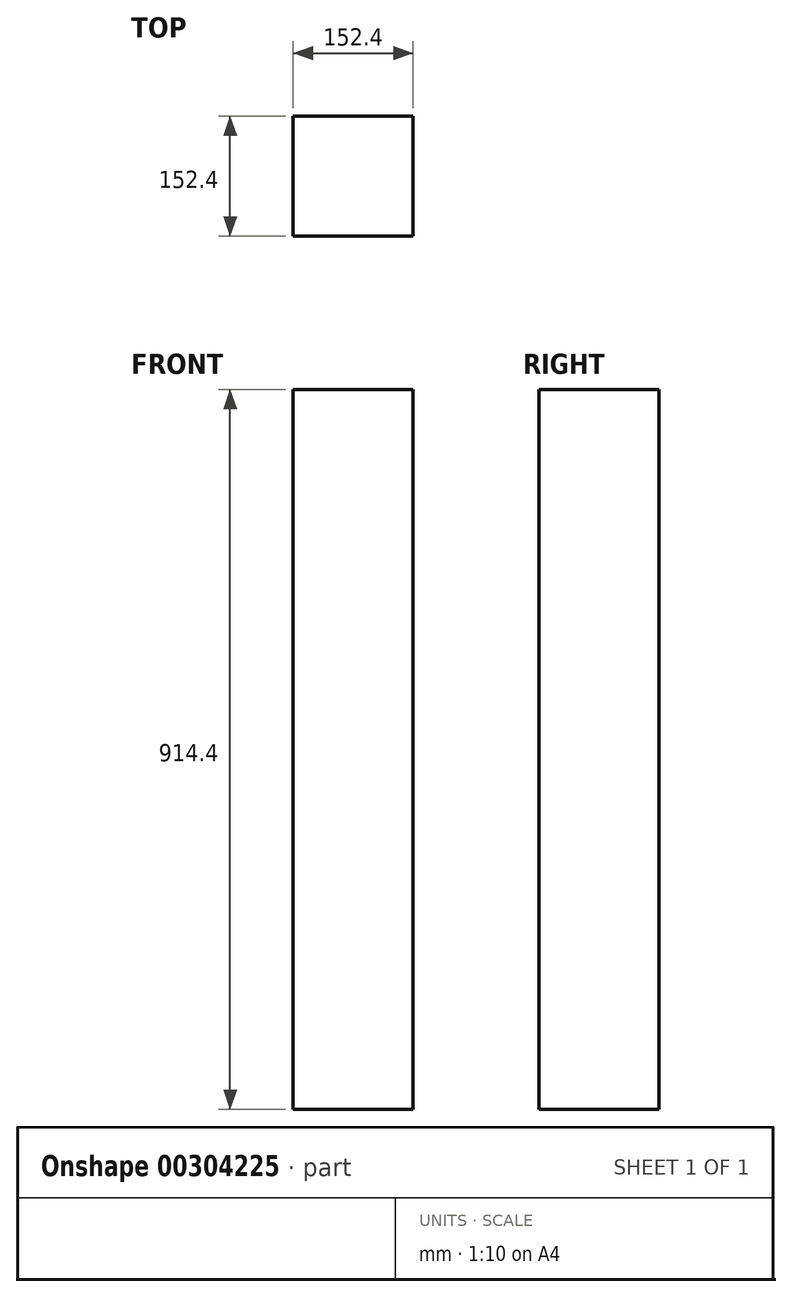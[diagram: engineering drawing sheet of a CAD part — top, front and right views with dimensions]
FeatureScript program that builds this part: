
annotation { "Feature Type Name" : "Feature", "Feature Type Description" : "" }
export const myFeature = defineFeature(function(context is Context, id is Id, definition is map)
    precondition{}
    {
        {
            var Q0;
            Q0=qCreatedBy(makeId("Top.planeOp"),FACE);
            var sketch = newSketch(context, id + "F0", { "sketchPlane" : qUnion([Q0])});
            skLineSegment(sketch, "E0.bottom", {"start": v(-76.2, -76.2) * mm, "end": v(76.2, -76.2) * mm});
            skLineSegment(sketch, "E0.top", {"start": v(-76.2, 76.2) * mm, "end": v(76.2, 76.2) * mm});
            skLineSegment(sketch, "E0.left", {"start": v(-76.2, -76.2) * mm, "end": v(-76.2, 76.2) * mm});
            skLineSegment(sketch, "E0.right", {"start": v(76.2, -76.2) * mm, "end": v(76.2, 76.2) * mm});
            skPoint(sketch, "E0.middle", {"position": v(0, 0) * mm});
            skSolve(sketch);
        }
        {
            var Q0;
            Q0=makeQuery(id+"F0.imprint","IMPRINT",FACE,{"disambiguationData":[TD([[makeQuery(id+"F0.imprint","IMPRINT",EDGE,{"derivedFrom":sQuery(id+"F0.wireOp",EDGE,"E0.bottom")}),1.0]])]});
            extrude(context, id + "F1", {"entities" : qUnion([Q0]), "endBound" : BoundingType.SYMMETRIC, "oppositeDirection" : true, "depth" : 914.4 * mm});
        }
    });
